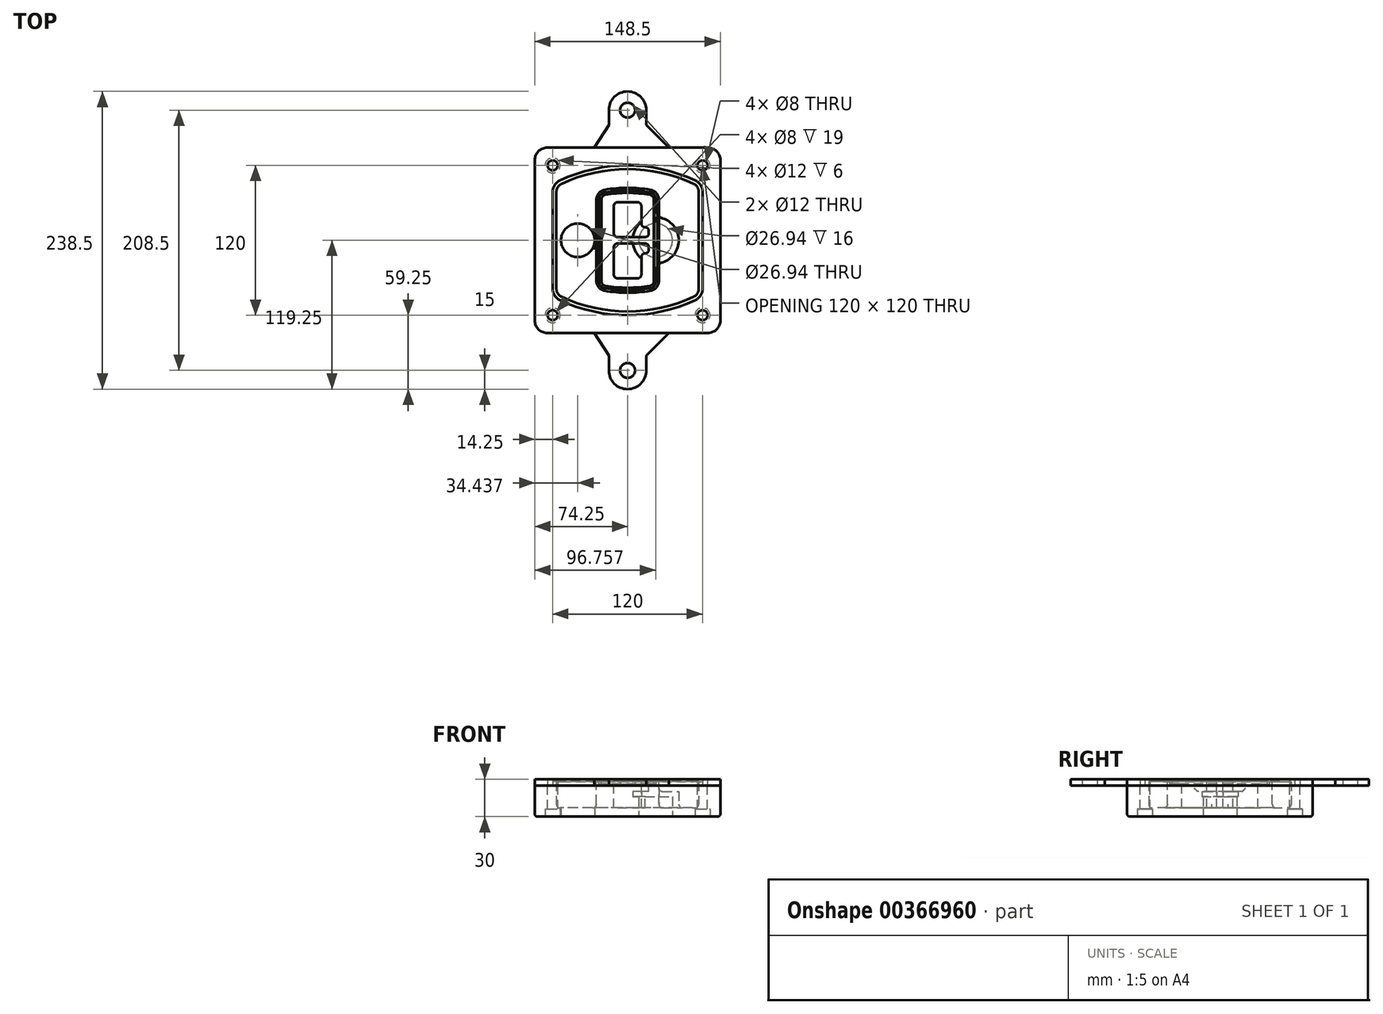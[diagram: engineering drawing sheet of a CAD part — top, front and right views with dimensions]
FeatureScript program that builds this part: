
annotation { "Feature Type Name" : "Feature", "Feature Type Description" : "" }
export const myFeature = defineFeature(function(context is Context, id is Id, definition is map)
    precondition{}
    {
        {
            var Q0;
            Q0=qCreatedBy(makeId("Top.planeOp"),FACE);
            var sketch = newSketch(context, id + "F0", { "sketchPlane" : qUnion([Q0])});
            skPoint(sketch, "E0.rect.middle", {"position": v(0, 0) * mm});
            skLineSegment(sketch, "E1.bottom", {"start": v(-64.25, -74.25) * mm, "end": v(64.25, -74.25) * mm});
            skLineSegment(sketch, "E1.top", {"start": v(-64.25, 74.25) * mm, "end": v(64.25, 74.25) * mm});
            skLineSegment(sketch, "E1.left", {"start": v(-74.25, -64.25) * mm, "end": v(-74.25, 64.25) * mm});
            skLineSegment(sketch, "E1.right", {"start": v(74.25, -64.25) * mm, "end": v(74.25, 64.25) * mm});
            skLineSegment(sketch, "E2", {"start": v(-74.25, 74.25) * mm, "end": v(74.25, -74.25) * mm, "construction": true});
            skLineSegment(sketch, "E3", {"start": v(74.25, 74.25) * mm, "end": v(-74.25, -74.25) * mm, "construction": true});
            skCircle(sketch, "E4", {"center": v(-60, 60) * mm, "radius": 4 * mm});
            skCircle(sketch, "E5", {"center": v(60, 60) * mm, "radius": 4 * mm});
            skCircle(sketch, "E6", {"center": v(60, -60) * mm, "radius": 4 * mm});
            skCircle(sketch, "E7", {"center": v(-60, -60) * mm, "radius": 4 * mm});
            skLineSegment(sketch, "E8", {"start": v(-60, 60) * mm, "end": v(60, 60) * mm, "construction": true});
            skLineSegment(sketch, "E9", {"start": v(60, 60) * mm, "end": v(60, -60) * mm, "construction": true});
            skLineSegment(sketch, "E10", {"start": v(60, -60) * mm, "end": v(-60, -60) * mm, "construction": true});
            skLineSegment(sketch, "E11", {"start": v(-60, -60) * mm, "end": v(-60, 60) * mm, "construction": true});
            skLineSegment(sketch, "E12", {"start": v(-60, 38.83) * mm, "end": v(-60, -38.83) * mm});
            skLineSegment(sketch, "E13", {"start": v(60, 38.83) * mm, "end": v(60, -38.83) * mm});
            skArc(sketch, "E14", {"start": v(54.26, 47.88) * mm, "mid": v(0, 60) * mm, "end": v(-54.26, 47.88) * mm});
            skArc(sketch, "E15", {"start": v(-54.26, -47.88) * mm, "mid": v(0, -60) * mm, "end": v(54.26, -47.88) * mm});
            skLineSegment(sketch, "E16", {"start": v(-60, 0) * mm, "end": v(60, 0) * mm, "construction": true});
            skPoint(sketch, "E17.visualSharp", {"position": v(-60, -45) * mm});
            skArc(sketch, "E17.filletArc", {"start": v(-60, -38.83) * mm, "mid": v(-58.44, -44.2) * mm, "end": v(-54.26, -47.88) * mm});
            skPoint(sketch, "E18.visualSharp", {"position": v(-60, 45) * mm});
            skArc(sketch, "E18.filletArc", {"start": v(-54.26, 47.88) * mm, "mid": v(-58.44, 44.2) * mm, "end": v(-60, 38.83) * mm});
            skPoint(sketch, "E19.visualSharp", {"position": v(60, 45) * mm});
            skArc(sketch, "E19.filletArc", {"start": v(60, 38.83) * mm, "mid": v(58.44, 44.2) * mm, "end": v(54.26, 47.88) * mm});
            skPoint(sketch, "E20.visualSharp", {"position": v(60, -45) * mm});
            skArc(sketch, "E20.filletArc", {"start": v(54.26, -47.88) * mm, "mid": v(58.44, -44.2) * mm, "end": v(60, -38.83) * mm});
            skPoint(sketch, "E21.visualSharp", {"position": v(-74.25, 74.25) * mm});
            skArc(sketch, "E21.filletArc", {"start": v(-64.25, 74.25) * mm, "mid": v(-71.32, 71.32) * mm, "end": v(-74.25, 64.25) * mm});
            skPoint(sketch, "E22.visualSharp", {"position": v(74.25, 74.25) * mm});
            skArc(sketch, "E22.filletArc", {"start": v(74.25, 64.25) * mm, "mid": v(71.32, 71.32) * mm, "end": v(64.25, 74.25) * mm});
            skPoint(sketch, "E23.visualSharp", {"position": v(74.25, -74.25) * mm});
            skArc(sketch, "E23.filletArc", {"start": v(64.25, -74.25) * mm, "mid": v(71.32, -71.32) * mm, "end": v(74.25, -64.25) * mm});
            skPoint(sketch, "E24.visualSharp", {"position": v(-74.25, -74.25) * mm});
            skArc(sketch, "E24.filletArc", {"start": v(-74.25, -64.25) * mm, "mid": v(-71.32, -71.32) * mm, "end": v(-64.25, -74.25) * mm});
            skArc(sketch, "E25.0", {"start": v(57, 38.83) * mm, "mid": v(55.9, 42.58) * mm, "end": v(52.98, 45.17) * mm});
            skLineSegment(sketch, "E25.1", {"start": v(57, 38.83) * mm, "end": v(57, -38.83) * mm});
            skArc(sketch, "E25.2", {"start": v(52.98, -45.17) * mm, "mid": v(55.9, -42.58) * mm, "end": v(57, -38.83) * mm});
            skArc(sketch, "E25.3", {"start": v(-52.98, -45.17) * mm, "mid": v(0, -57) * mm, "end": v(52.98, -45.17) * mm});
            skArc(sketch, "E25.4", {"start": v(-57, -38.83) * mm, "mid": v(-55.9, -42.58) * mm, "end": v(-52.98, -45.17) * mm});
            skArc(sketch, "E25.5", {"start": v(52.98, 45.17) * mm, "mid": v(0, 57) * mm, "end": v(-52.98, 45.17) * mm});
            skLineSegment(sketch, "E25.6", {"start": v(-57, 38.83) * mm, "end": v(-57, -38.83) * mm});
            skArc(sketch, "E25.7", {"start": v(-52.98, 45.17) * mm, "mid": v(-55.9, 42.58) * mm, "end": v(-57, 38.83) * mm});
            skArc(sketch, "E26.0", {"start": v(-55.96, 51.5) * mm, "mid": v(-61.82, 46.33) * mm, "end": v(-64, 38.83) * mm});
            skArc(sketch, "E26.1", {"start": v(55.96, 51.5) * mm, "mid": v(0, 64) * mm, "end": v(-55.96, 51.5) * mm});
            skArc(sketch, "E26.2", {"start": v(64, 38.83) * mm, "mid": v(61.82, 46.33) * mm, "end": v(55.96, 51.5) * mm});
            skLineSegment(sketch, "E26.3", {"start": v(64, 38.83) * mm, "end": v(64, -38.83) * mm});
            skArc(sketch, "E26.4", {"start": v(55.96, -51.5) * mm, "mid": v(61.82, -46.33) * mm, "end": v(64, -38.83) * mm});
            skLineSegment(sketch, "E26.5", {"start": v(-64, 38.83) * mm, "end": v(-64, -38.83) * mm});
            skArc(sketch, "E26.6", {"start": v(-55.96, -51.5) * mm, "mid": v(0, -64) * mm, "end": v(55.96, -51.5) * mm});
            skArc(sketch, "E26.7", {"start": v(-64, -38.83) * mm, "mid": v(-61.82, -46.33) * mm, "end": v(-55.96, -51.5) * mm});
            skSolve(sketch);
        }
        {
            var Q0;
            Q0=makeQuery(id+"F0.imprint","IMPRINT",FACE,{"disambiguationData":[TD([[makeQuery(id+"F0.imprint","IMPRINT",EDGE,{"derivedFrom":sQuery(id+"F0.wireOp",EDGE,"E1.bottom")}),1.0]])]});
            var Q1;
            Q1=makeQuery(id+"F0.imprint","IMPRINT",FACE,{"disambiguationData":[TD([[makeQuery(id+"F0.imprint","IMPRINT",EDGE,{"derivedFrom":sQuery(id+"F0.wireOp",EDGE,"E12")}),1.0]])]});
            var Q2;
            Q2=makeQuery(id+"F0.imprint","IMPRINT",FACE,{"disambiguationData":[TD([[makeQuery(id+"F0.imprint","IMPRINT",EDGE,{"derivedFrom":sQuery(id+"F0.wireOp",EDGE,"E25.0")}),1.0]])]});
            var Q3;
            Q3=makeQuery(id+"F0.imprint","IMPRINT",FACE,{"disambiguationData":[TD([[makeQuery(id+"F0.imprint","IMPRINT",EDGE,{"derivedFrom":sQuery(id+"F0.wireOp",EDGE,"E12")}),-1.0]])]});
            extrude(context, id + "F1", {"entities" : qUnion([Q0, Q1, Q2, Q3]), "oppositeDirection" : true, "depth" : 25 * mm});
        }
        {
            var Q0;
            Q0=makeQuery(id+"F0.imprint","IMPRINT",FACE,{"disambiguationData":[TD([[makeQuery(id+"F0.imprint","IMPRINT",EDGE,{"derivedFrom":sQuery(id+"F0.wireOp",EDGE,"E12")}),1.0]])]});
            extrude(context, id + "F2", {"entities" : qUnion([Q0]), "operationType" : NewBodyOperationType.ADD, "depth" : 3 * mm});
        }
        {
            var Q0;
            Q0=makeQuery(id+"F0.imprint","IMPRINT",FACE,{"disambiguationData":[TD([[makeQuery(id+"F0.imprint","IMPRINT",EDGE,{"derivedFrom":sQuery(id+"F0.wireOp",EDGE,"E25.0")}),1.0]])]});
            extrude(context, id + "F3", {"entities" : qUnion([Q0]), "operationType" : NewBodyOperationType.REMOVE, "oppositeDirection" : true, "depth" : 18 * mm});
        }
        {
            var Q0;
            Q0=makeQuery(id+"F2.opExtrude","CAP_FACE",FACE,{"disambiguationData":[OSD([sQuery(id+"F0.wireOp",EDGE,"E12"),sQuery(id+"F0.wireOp",EDGE,"E13"),sQuery(id+"F0.wireOp",EDGE,"E14"),sQuery(id+"F0.wireOp",EDGE,"E15"),sQuery(id+"F0.wireOp",EDGE,"E17.filletArc"),sQuery(id+"F0.wireOp",EDGE,"E18.filletArc"),sQuery(id+"F0.wireOp",EDGE,"E19.filletArc"),sQuery(id+"F0.wireOp",EDGE,"E20.filletArc"),sQuery(id+"F0.wireOp",EDGE,"E25.0"),sQuery(id+"F0.wireOp",EDGE,"E25.1"),sQuery(id+"F0.wireOp",EDGE,"E25.2"),sQuery(id+"F0.wireOp",EDGE,"E25.3"),sQuery(id+"F0.wireOp",EDGE,"E25.4"),sQuery(id+"F0.wireOp",EDGE,"E25.5"),sQuery(id+"F0.wireOp",EDGE,"E25.6"),sQuery(id+"F0.wireOp",EDGE,"E25.7")])],"isStart":false});
            var sketch = newSketch(context, id + "F4", { "sketchPlane" : qUnion([Q0])});
            skArc(sketch, "E27.0", {"start": v(-18.34, -40.45) * mm, "mid": v(0, -42) * mm, "end": v(18.34, -40.45) * mm});
            skArc(sketch, "E28.0", {"start": v(18.34, 40.45) * mm, "mid": v(0, 42) * mm, "end": v(-18.34, 40.45) * mm});
            skLineSegment(sketch, "E29", {"start": v(-25, 32.57) * mm, "end": v(-25, -32.57) * mm});
            skLineSegment(sketch, "E30", {"start": v(25, 32.57) * mm, "end": v(25, -32.57) * mm});
            skLineSegment(sketch, "E31", {"start": v(-25, 39.1) * mm, "end": v(25, 39.1) * mm, "construction": true});
            skLineSegment(sketch, "E32", {"start": v(-25, -39.1) * mm, "end": v(25, -39.1) * mm, "construction": true});
            skPoint(sketch, "E33.visualSharp", {"position": v(-25, 39.1) * mm});
            skArc(sketch, "E33.filletArc", {"start": v(-18.34, 40.45) * mm, "mid": v(-23.11, 37.73) * mm, "end": v(-25, 32.57) * mm});
            skPoint(sketch, "E34.visualSharp", {"position": v(25, 39.1) * mm});
            skArc(sketch, "E34.filletArc", {"start": v(25, 32.57) * mm, "mid": v(23.11, 37.73) * mm, "end": v(18.34, 40.45) * mm});
            skPoint(sketch, "E35.visualSharp", {"position": v(25, -39.1) * mm});
            skArc(sketch, "E35.filletArc", {"start": v(18.34, -40.45) * mm, "mid": v(23.11, -37.73) * mm, "end": v(25, -32.57) * mm});
            skPoint(sketch, "E36.visualSharp", {"position": v(-25, -39.1) * mm});
            skArc(sketch, "E36.filletArc", {"start": v(-25, -32.57) * mm, "mid": v(-23.11, -37.73) * mm, "end": v(-18.34, -40.45) * mm});
            skArc(sketch, "E37.0", {"start": v(52.98, 45.17) * mm, "mid": v(0, 57) * mm, "end": v(-52.98, 45.17) * mm});
            skArc(sketch, "E37.1", {"start": v(-52.98, 45.17) * mm, "mid": v(-55.9, 42.58) * mm, "end": v(-57, 38.83) * mm});
            skLineSegment(sketch, "E37.2", {"start": v(-57, 38.83) * mm, "end": v(-57, -38.83) * mm});
            skArc(sketch, "E37.3", {"start": v(-57, -38.83) * mm, "mid": v(-55.9, -42.58) * mm, "end": v(-52.98, -45.17) * mm});
            skArc(sketch, "E37.4", {"start": v(-52.98, -45.17) * mm, "mid": v(0, -57) * mm, "end": v(52.98, -45.17) * mm});
            skArc(sketch, "E37.5", {"start": v(52.98, -45.17) * mm, "mid": v(55.9, -42.58) * mm, "end": v(57, -38.83) * mm});
            skLineSegment(sketch, "E37.6", {"start": v(57, 38.83) * mm, "end": v(57, -38.83) * mm});
            skArc(sketch, "E37.7", {"start": v(57, 38.83) * mm, "mid": v(55.9, 42.58) * mm, "end": v(52.98, 45.17) * mm});
            skLineSegment(sketch, "E38.0", {"start": v(23, 32.57) * mm, "end": v(23, -32.57) * mm});
            skArc(sketch, "E38.1", {"start": v(18, -38.48) * mm, "mid": v(21.58, -36.44) * mm, "end": v(23, -32.57) * mm});
            skArc(sketch, "E38.2", {"start": v(-18, -38.48) * mm, "mid": v(0, -40) * mm, "end": v(18, -38.48) * mm});
            skArc(sketch, "E38.3", {"start": v(-23, -32.57) * mm, "mid": v(-21.58, -36.44) * mm, "end": v(-18, -38.48) * mm});
            skLineSegment(sketch, "E38.4", {"start": v(-23, 32.57) * mm, "end": v(-23, -32.57) * mm});
            skArc(sketch, "E38.5", {"start": v(23, 32.57) * mm, "mid": v(21.58, 36.44) * mm, "end": v(18, 38.48) * mm});
            skArc(sketch, "E38.6", {"start": v(-18, 38.48) * mm, "mid": v(-21.58, 36.44) * mm, "end": v(-23, 32.57) * mm});
            skArc(sketch, "E38.7", {"start": v(18, 38.48) * mm, "mid": v(0, 40) * mm, "end": v(-18, 38.48) * mm});
            skArc(sketch, "E39.0", {"start": v(21, 32.57) * mm, "mid": v(20.06, 35.15) * mm, "end": v(17.67, 36.5) * mm});
            skLineSegment(sketch, "E39.1", {"start": v(21, 32.57) * mm, "end": v(21, -32.57) * mm});
            skArc(sketch, "E39.2", {"start": v(17.67, -36.5) * mm, "mid": v(20.06, -35.15) * mm, "end": v(21, -32.57) * mm});
            skArc(sketch, "E39.3", {"start": v(-17.67, -36.5) * mm, "mid": v(0, -38) * mm, "end": v(17.67, -36.5) * mm});
            skArc(sketch, "E39.4", {"start": v(-21, -32.57) * mm, "mid": v(-20.06, -35.15) * mm, "end": v(-17.67, -36.5) * mm});
            skArc(sketch, "E39.5", {"start": v(17.67, 36.5) * mm, "mid": v(0, 38) * mm, "end": v(-17.67, 36.5) * mm});
            skLineSegment(sketch, "E39.6", {"start": v(-21, 32.57) * mm, "end": v(-21, -32.57) * mm});
            skArc(sketch, "E39.7", {"start": v(-17.67, 36.5) * mm, "mid": v(-20.06, 35.15) * mm, "end": v(-21, 32.57) * mm});
            skLineSegment(sketch, "E40", {"start": v(-25, 0) * mm, "end": v(25, 0) * mm, "construction": true});
            skLineSegment(sketch, "E41", {"start": v(-11, 5.5) * mm, "end": v(-11, 27.5) * mm});
            skLineSegment(sketch, "E42", {"start": v(-8, 30.5) * mm, "end": v(8, 30.5) * mm});
            skLineSegment(sketch, "E43", {"start": v(11, 27.5) * mm, "end": v(11, 13.5) * mm});
            skLineSegment(sketch, "E44", {"start": v(14, 10.5) * mm, "end": v(14, 10.5) * mm});
            skLineSegment(sketch, "E45", {"start": v(17, 7.5) * mm, "end": v(17, 5.5) * mm});
            skLineSegment(sketch, "E46", {"start": v(14, 2.5) * mm, "end": v(-8, 2.5) * mm});
            skPoint(sketch, "E47.visualSharp", {"position": v(-11, 30.5) * mm});
            skArc(sketch, "E47.filletArc", {"start": v(-8, 30.5) * mm, "mid": v(-10.12, 29.62) * mm, "end": v(-11, 27.5) * mm});
            skPoint(sketch, "E48.visualSharp", {"position": v(11, 30.5) * mm});
            skArc(sketch, "E48.filletArc", {"start": v(11, 27.5) * mm, "mid": v(10.12, 29.62) * mm, "end": v(8, 30.5) * mm});
            skPoint(sketch, "E49.visualSharp", {"position": v(11, 10.5) * mm});
            skArc(sketch, "E49.filletArc", {"start": v(11, 13.5) * mm, "mid": v(11.88, 11.38) * mm, "end": v(14, 10.5) * mm});
            skPoint(sketch, "E50.visualSharp", {"position": v(17, 10.5) * mm});
            skArc(sketch, "E50.filletArc", {"start": v(17, 7.5) * mm, "mid": v(16.12, 9.62) * mm, "end": v(14, 10.5) * mm});
            skPoint(sketch, "E51.visualSharp", {"position": v(17, 2.5) * mm});
            skArc(sketch, "E51.filletArc", {"start": v(14, 2.5) * mm, "mid": v(16.12, 3.38) * mm, "end": v(17, 5.5) * mm});
            skPoint(sketch, "E52.visualSharp", {"position": v(-11, 2.5) * mm});
            skArc(sketch, "E52.filletArc", {"start": v(-11, 5.5) * mm, "mid": v(-10.12, 3.38) * mm, "end": v(-8, 2.5) * mm});
            skLineSegment(sketch, "E53.0.MirrorCS", {"start": v(14, -2.5) * mm, "end": v(-8, -2.5) * mm});
            skArc(sketch, "E54.0.MirrorCS", {"start": v(-11, -5.5) * mm, "mid": v(-10.12, -3.38) * mm, "end": v(-8, -2.5) * mm});
            skLineSegment(sketch, "E55.0.MirrorCS", {"start": v(-11, -5.5) * mm, "end": v(-11, -27.5) * mm});
            skArc(sketch, "E56.0.MirrorCS", {"start": v(-8, -30.5) * mm, "mid": v(-10.12, -29.62) * mm, "end": v(-11, -27.5) * mm});
            skLineSegment(sketch, "E57.0.MirrorCS", {"start": v(-8, -30.5) * mm, "end": v(8, -30.5) * mm});
            skArc(sketch, "E58.0.MirrorCS", {"start": v(11, -27.5) * mm, "mid": v(10.12, -29.62) * mm, "end": v(8, -30.5) * mm});
            skLineSegment(sketch, "E59.0.MirrorCS", {"start": v(11, -27.5) * mm, "end": v(11, -13.5) * mm});
            skArc(sketch, "E60.0.MirrorCS", {"start": v(11, -13.5) * mm, "mid": v(11.88, -11.38) * mm, "end": v(14, -10.5) * mm});
            skArc(sketch, "E61.0.MirrorCS", {"start": v(17, -7.5) * mm, "mid": v(16.12, -9.62) * mm, "end": v(14, -10.5) * mm});
            skLineSegment(sketch, "E62.0.MirrorCS", {"start": v(17, -7.5) * mm, "end": v(17, -5.5) * mm});
            skArc(sketch, "E63.0.MirrorCS", {"start": v(14, -2.5) * mm, "mid": v(16.12, -3.38) * mm, "end": v(17, -5.5) * mm});
            skSolve(sketch);
        }
        {
            var Q0;
            Q0=makeQuery(id+"F4.imprint","IMPRINT",FACE,{"disambiguationData":[TD([[makeQuery(id+"F4.imprint","IMPRINT",EDGE,{"derivedFrom":sQuery(id+"F4.wireOp",EDGE,"E27.0")}),1.0]])]});
            var Q1;
            Q1=makeQuery(id+"F4.imprint","IMPRINT",FACE,{"disambiguationData":[TD([[makeQuery(id+"F4.imprint","IMPRINT",EDGE,{"derivedFrom":sQuery(id+"F4.wireOp",EDGE,"E38.0")}),-1.0]])]});
            var Q2;
            Q2=makeQuery(id+"F4.imprint","IMPRINT",FACE,{"disambiguationData":[TD([[makeQuery(id+"F4.imprint","IMPRINT",EDGE,{"derivedFrom":sQuery(id+"F4.wireOp",EDGE,"E39.0")}),1.0]])]});
            extrude(context, id + "F5", {"entities" : qUnion([Q0, Q1, Q2]), "operationType" : NewBodyOperationType.ADD, "endBound" : BoundingType.UP_TO_NEXT, "oppositeDirection" : true, "depth" : 25 * mm});
        }
        {
            var Q0;
            Q0=makeQuery(id+"F4.imprint","IMPRINT",FACE,{"disambiguationData":[TD([[makeQuery(id+"F4.imprint","IMPRINT",EDGE,{"derivedFrom":sQuery(id+"F4.wireOp",EDGE,"E38.0")}),-1.0]])]});
            extrude(context, id + "F6", {"entities" : qUnion([Q0]), "operationType" : NewBodyOperationType.REMOVE, "oppositeDirection" : true, "depth" : 2 * mm});
        }
        {
            var Q0;
            Q0=makeQuery(id+"F1.opExtrude","CAP_FACE",FACE,{"disambiguationData":[OSD([sQuery(id+"F0.wireOp",EDGE,"E1.bottom"),sQuery(id+"F0.wireOp",EDGE,"E1.top"),sQuery(id+"F0.wireOp",EDGE,"E1.left"),sQuery(id+"F0.wireOp",EDGE,"E1.right"),sQuery(id+"F0.wireOp",EDGE,"E4"),sQuery(id+"F0.wireOp",EDGE,"E5"),sQuery(id+"F0.wireOp",EDGE,"E6"),sQuery(id+"F0.wireOp",EDGE,"E7"),sQuery(id+"F0.wireOp",EDGE,"E21.filletArc"),sQuery(id+"F0.wireOp",EDGE,"E22.filletArc"),sQuery(id+"F0.wireOp",EDGE,"E23.filletArc"),sQuery(id+"F0.wireOp",EDGE,"E24.filletArc")])],"isStart":false});
            var sketch = newSketch(context, id + "F7", { "sketchPlane" : qUnion([Q0])});
            skCircle(sketch, "E64", {"center": v(22.5, 0) * mm, "radius": 13.47 * mm});
            skCircle(sketch, "E65", {"center": v(-39.81, 0) * mm, "radius": 13.47 * mm});
            skLineSegment(sketch, "E66", {"start": v(74.25, 0) * mm, "end": v(-74.25, 0) * mm});
            skCircle(sketch, "E67", {"center": v(22.5, 0) * mm, "radius": 18.47 * mm});
            skCircle(sketch, "E68", {"center": v(60, -60) * mm, "radius": 6 * mm});
            skCircle(sketch, "E69", {"center": v(-60, -60) * mm, "radius": 6 * mm});
            skCircle(sketch, "E70", {"center": v(-60, 60) * mm, "radius": 6 * mm});
            skCircle(sketch, "E71", {"center": v(60, 60) * mm, "radius": 6 * mm});
            skSolve(sketch);
        }
        {
            var Q0;
            {var subQ1=sQuery(id+"F7.wireOp",EDGE,"E66");var subQ4=sQuery(id+"F7.wireOp",EDGE,"E64");var subQ6=makeQuery(id+"F7.imprint","INTERSECT",VERTEX,{"disambiguationData":[OD(0.0)],"derivedFrom":[subQ4,subQ1]});Q0=makeQuery(id+"F7.imprint","IMPRINT",FACE,{"disambiguationData":[TD([[makeQuery(id+"F7.imprint","IMPRINT",EDGE,{"disambiguationData":[TD([[subQ6,-1.0]])],"derivedFrom":subQ4}),-1.0]])]});}
            var Q1;
            {var subQ0=sQuery(id+"F7.wireOp",EDGE,"E66");var subQ1=sQuery(id+"F7.wireOp",EDGE,"E64");var subQ3=makeQuery(id+"F7.imprint","INTERSECT",VERTEX,{"disambiguationData":[OD(0.0)],"derivedFrom":[subQ1,subQ0]});Q1=makeQuery(id+"F7.imprint","IMPRINT",FACE,{"disambiguationData":[TD([[makeQuery(id+"F7.imprint","IMPRINT",EDGE,{"disambiguationData":[TD([[subQ3,-1.0]])],"derivedFrom":subQ1}),1.0]])]});}
            var Q2;
            {var subQ0=sQuery(id+"F7.wireOp",EDGE,"E66");var subQ1=sQuery(id+"F7.wireOp",EDGE,"E64");var subQ3=makeQuery(id+"F7.imprint","INTERSECT",VERTEX,{"disambiguationData":[OD(0.0)],"derivedFrom":[subQ1,subQ0]});Q2=makeQuery(id+"F7.imprint","IMPRINT",FACE,{"disambiguationData":[TD([[makeQuery(id+"F7.imprint","IMPRINT",EDGE,{"disambiguationData":[TD([[subQ3,1.0]])],"derivedFrom":subQ1}),1.0]])]});}
            var Q3;
            {var subQ1=sQuery(id+"F7.wireOp",EDGE,"E66");var subQ4=sQuery(id+"F7.wireOp",EDGE,"E64");var subQ6=makeQuery(id+"F7.imprint","INTERSECT",VERTEX,{"disambiguationData":[OD(0.0)],"derivedFrom":[subQ4,subQ1]});Q3=makeQuery(id+"F7.imprint","IMPRINT",FACE,{"disambiguationData":[TD([[makeQuery(id+"F7.imprint","IMPRINT",EDGE,{"disambiguationData":[TD([[subQ6,1.0]])],"derivedFrom":subQ4}),-1.0]])]});}
            extrude(context, id + "F8", {"entities" : qUnion([Q0, Q1, Q2, Q3]), "operationType" : NewBodyOperationType.ADD, "oppositeDirection" : true, "depth" : 20 * mm});
        }
        {
            var Q0;
            {var subQ0=sQuery(id+"F7.wireOp",EDGE,"E66");var subQ1=sQuery(id+"F7.wireOp",EDGE,"E64");var subQ3=makeQuery(id+"F7.imprint","INTERSECT",VERTEX,{"disambiguationData":[OD(0.0)],"derivedFrom":[subQ1,subQ0]});Q0=makeQuery(id+"F7.imprint","IMPRINT",FACE,{"disambiguationData":[TD([[makeQuery(id+"F7.imprint","IMPRINT",EDGE,{"disambiguationData":[TD([[subQ3,-1.0]])],"derivedFrom":subQ1}),1.0]])]});}
            var Q1;
            {var subQ0=sQuery(id+"F7.wireOp",EDGE,"E66");var subQ1=sQuery(id+"F7.wireOp",EDGE,"E64");var subQ3=makeQuery(id+"F7.imprint","INTERSECT",VERTEX,{"disambiguationData":[OD(0.0)],"derivedFrom":[subQ1,subQ0]});Q1=makeQuery(id+"F7.imprint","IMPRINT",FACE,{"disambiguationData":[TD([[makeQuery(id+"F7.imprint","IMPRINT",EDGE,{"disambiguationData":[TD([[subQ3,1.0]])],"derivedFrom":subQ1}),1.0]])]});}
            extrude(context, id + "F9", {"entities" : qUnion([Q0, Q1]), "operationType" : NewBodyOperationType.REMOVE, "oppositeDirection" : true, "depth" : 16 * mm});
        }
        {
            var Q0;
            {var subQ0=sQuery(id+"F7.wireOp",EDGE,"E66");var subQ1=sQuery(id+"F7.wireOp",EDGE,"E65");var subQ3=makeQuery(id+"F7.imprint","INTERSECT",VERTEX,{"disambiguationData":[OD(0.0)],"derivedFrom":[subQ1,subQ0]});Q0=makeQuery(id+"F7.imprint","IMPRINT",FACE,{"disambiguationData":[TD([[makeQuery(id+"F7.imprint","IMPRINT",EDGE,{"disambiguationData":[TD([[subQ3,-1.0]])],"derivedFrom":subQ1}),1.0]])]});}
            var Q1;
            {var subQ0=sQuery(id+"F7.wireOp",EDGE,"E66");var subQ1=sQuery(id+"F7.wireOp",EDGE,"E65");var subQ3=makeQuery(id+"F7.imprint","INTERSECT",VERTEX,{"disambiguationData":[OD(0.0)],"derivedFrom":[subQ1,subQ0]});Q1=makeQuery(id+"F7.imprint","IMPRINT",FACE,{"disambiguationData":[TD([[makeQuery(id+"F7.imprint","IMPRINT",EDGE,{"disambiguationData":[TD([[subQ3,1.0]])],"derivedFrom":subQ1}),1.0]])]});}
            extrude(context, id + "F10", {"entities" : qUnion([Q0, Q1]), "operationType" : NewBodyOperationType.REMOVE, "oppositeDirection" : true, "depth" : 25 * mm});
        }
        {
            var Q0;
            Q0=makeQuery(id+"F7.imprint","IMPRINT",FACE,{"disambiguationData":[TD([[makeQuery(id+"F7.imprint","IMPRINT",EDGE,{"derivedFrom":sQuery(id+"F7.wireOp",EDGE,"E68")}),1.0]])]});
            var Q1;
            Q1=makeQuery(id+"F7.imprint","IMPRINT",FACE,{"disambiguationData":[TD([[makeQuery(id+"F7.imprint","IMPRINT",EDGE,{"derivedFrom":makeQuery(id+"F1.opExtrude","CAP_EDGE",EDGE,{"disambiguationData":[OSD([sQuery(id+"F0.wireOp",EDGE,"E5")])],"isStart":false})}),-1.0]])]});
            var Q2;
            Q2=makeQuery(id+"F7.imprint","IMPRINT",FACE,{"disambiguationData":[TD([[makeQuery(id+"F7.imprint","IMPRINT",EDGE,{"derivedFrom":sQuery(id+"F7.wireOp",EDGE,"E69")}),1.0]])]});
            var Q3;
            Q3=makeQuery(id+"F7.imprint","IMPRINT",FACE,{"disambiguationData":[TD([[makeQuery(id+"F7.imprint","IMPRINT",EDGE,{"derivedFrom":makeQuery(id+"F1.opExtrude","CAP_EDGE",EDGE,{"disambiguationData":[OSD([sQuery(id+"F0.wireOp",EDGE,"E4")])],"isStart":false})}),-1.0]])]});
            var Q4;
            Q4=makeQuery(id+"F7.imprint","IMPRINT",FACE,{"disambiguationData":[TD([[makeQuery(id+"F7.imprint","IMPRINT",EDGE,{"derivedFrom":sQuery(id+"F7.wireOp",EDGE,"E70")}),1.0]])]});
            var Q5;
            Q5=makeQuery(id+"F7.imprint","IMPRINT",FACE,{"disambiguationData":[TD([[makeQuery(id+"F7.imprint","IMPRINT",EDGE,{"derivedFrom":makeQuery(id+"F1.opExtrude","CAP_EDGE",EDGE,{"disambiguationData":[OSD([sQuery(id+"F0.wireOp",EDGE,"E7")])],"isStart":false})}),-1.0]])]});
            var Q6;
            Q6=makeQuery(id+"F7.imprint","IMPRINT",FACE,{"disambiguationData":[TD([[makeQuery(id+"F7.imprint","IMPRINT",EDGE,{"derivedFrom":sQuery(id+"F7.wireOp",EDGE,"E71")}),1.0]])]});
            var Q7;
            Q7=makeQuery(id+"F7.imprint","IMPRINT",FACE,{"disambiguationData":[TD([[makeQuery(id+"F7.imprint","IMPRINT",EDGE,{"derivedFrom":makeQuery(id+"F1.opExtrude","CAP_EDGE",EDGE,{"disambiguationData":[OSD([sQuery(id+"F0.wireOp",EDGE,"E6")])],"isStart":false})}),-1.0]])]});
            extrude(context, id + "F11", {"entities" : qUnion([Q0, Q1, Q2, Q3, Q4, Q5, Q6, Q7]), "operationType" : NewBodyOperationType.REMOVE, "oppositeDirection" : true, "depth" : 6 * mm});
        }
        {
            var Q0;
            Q0=makeQuery(id+"F9.boolean.opBoolean","COPY",FACE,{"derivedFrom":makeQuery(id+"F9.opExtrude","CAP_FACE",FACE,{"disambiguationData":[OSD([sQuery(id+"F7.wireOp",EDGE,"E64")])],"isStart":false})});
            var sketch = newSketch(context, id + "F12", { "sketchPlane" : qUnion([Q0])});
            skArc(sketch, "E72.0", {"start": v(11, 14.45) * mm, "mid": v(6.45, 9.13) * mm, "end": v(4.2, 2.5) * mm});
            skArc(sketch, "E72.1", {"start": v(4.2, -2.5) * mm, "mid": v(6.45, -9.13) * mm, "end": v(11, -14.45) * mm});
            skLineSegment(sketch, "E73", {"start": v(4.2, -2.5) * mm, "end": v(14, -2.5) * mm});
            skLineSegment(sketch, "E74.0", {"start": v(14, 2.5) * mm, "end": v(4.2, 2.5) * mm});
            skArc(sketch, "E74.1", {"start": v(14, 2.5) * mm, "mid": v(16.12, 3.38) * mm, "end": v(17, 5.5) * mm});
            skLineSegment(sketch, "E74.2", {"start": v(17, 7.5) * mm, "end": v(17, 5.5) * mm});
            skArc(sketch, "E74.3", {"start": v(17, 7.5) * mm, "mid": v(16.12, 9.62) * mm, "end": v(14, 10.5) * mm});
            skArc(sketch, "E74.4", {"start": v(11, 13.5) * mm, "mid": v(11.88, 11.38) * mm, "end": v(14, 10.5) * mm});
            skLineSegment(sketch, "E74.5", {"start": v(11, 14.45) * mm, "end": v(11, 13.5) * mm});
            skLineSegment(sketch, "E74.7", {"start": v(14, -2.5) * mm, "end": v(4.2, -2.5) * mm});
            skArc(sketch, "E74.8", {"start": v(14, -2.5) * mm, "mid": v(16.12, -3.38) * mm, "end": v(17, -5.5) * mm});
            skLineSegment(sketch, "E74.9", {"start": v(17, -7.5) * mm, "end": v(17, -5.5) * mm});
            skArc(sketch, "E74.10", {"start": v(17, -7.5) * mm, "mid": v(16.12, -9.62) * mm, "end": v(14, -10.5) * mm});
            skArc(sketch, "E74.11", {"start": v(11, -13.5) * mm, "mid": v(11.88, -11.38) * mm, "end": v(14, -10.5) * mm});
            skLineSegment(sketch, "E74.12", {"start": v(11, -14.45) * mm, "end": v(11, -13.5) * mm});
            skPoint(sketch, "E75.orphan", {"position": v(11, -27.5) * mm});
            skPoint(sketch, "E76.orphan", {"position": v(-8, -2.5) * mm});
            skPoint(sketch, "E77.orphan", {"position": v(-8, 2.5) * mm});
            skPoint(sketch, "E78.orphan", {"position": v(11, 27.5) * mm});
            skSolve(sketch);
        }
        {
            var Q0;
            {var subQ7=sQuery(id+"F12.wireOp",EDGE,"E72.0");var subQ14=sQuery(id+"F12.wireOp",EDGE,"E72.1");var subQ16=sQuery(id+"F12.wireOp",EDGE,"E74.1");var subQ18=sQuery(id+"F12.wireOp",EDGE,"E74.8");Q0=qUnion([makeQuery(id+"F12.imprint","IMPRINT",FACE,{"disambiguationData":[TD([[makeQuery(id+"F12.imprint","IMPRINT",EDGE,{"derivedFrom":subQ7}),1.0]])]}),makeQuery(id+"F12.imprint","IMPRINT",FACE,{"disambiguationData":[TD([[makeQuery(id+"F12.imprint","IMPRINT",EDGE,{"derivedFrom":subQ14}),1.0]])]}),makeQuery(id+"F12.imprint","IMPRINT",FACE,{"disambiguationData":[TD([[makeQuery(id+"F12.imprint","IMPRINT",EDGE,{"derivedFrom":subQ16}),1.0]])]}),makeQuery(id+"F12.imprint","IMPRINT",FACE,{"disambiguationData":[TD([[makeQuery(id+"F12.imprint","IMPRINT",EDGE,{"derivedFrom":subQ18}),-1.0]])]})]);}
            var Q1;
            Q1=makeQuery(id+"F5.boolean.opBoolean","SPLIT",FACE,{"disambiguationData":[TD([makeQuery(id+"F5.opExtrude","SWEPT_FACE",FACE,{"disambiguationData":[OSD([sQuery(id+"F4.wireOp",EDGE,"E41")])]})])],"derivedFrom":makeQuery(id+"F3.boolean.opBoolean","COPY",FACE,{"derivedFrom":makeQuery(id+"F3.opExtrude","CAP_FACE",FACE,{"disambiguationData":[OSD([sQuery(id+"F0.wireOp",EDGE,"E25.0"),sQuery(id+"F0.wireOp",EDGE,"E25.1"),sQuery(id+"F0.wireOp",EDGE,"E25.2"),sQuery(id+"F0.wireOp",EDGE,"E25.3"),sQuery(id+"F0.wireOp",EDGE,"E25.4"),sQuery(id+"F0.wireOp",EDGE,"E25.5"),sQuery(id+"F0.wireOp",EDGE,"E25.6"),sQuery(id+"F0.wireOp",EDGE,"E25.7")])],"isStart":false})})});
            extrude(context, id + "F13", {"entities" : qUnion([Q0]), "operationType" : NewBodyOperationType.REMOVE, "endBound" : BoundingType.UP_TO_SURFACE, "endBoundEntityFace" : qUnion([Q1]), "depth" : 25 * mm});
        }
        {
            var Q0;
            Q0=makeQuery(id+"F3.boolean.opBoolean","COPY",EDGE,{"derivedFrom":makeQuery(id+"F3.opExtrude","CAP_EDGE",EDGE,{"disambiguationData":[OSD([sQuery(id+"F0.wireOp",EDGE,"E25.6")])],"isStart":false})});
            var Q1;
            Q1=makeQuery(id+"F8.boolean.opBoolean","INTERSECT",EDGE,{"derivedFrom":[makeQuery(id+"F5.opExtrude","SWEPT_FACE",FACE,{"disambiguationData":[OSD([sQuery(id+"F4.wireOp",EDGE,"E30")])]}),makeQuery(id+"F8.opExtrude","CAP_FACE",FACE,{"disambiguationData":[OSD([sQuery(id+"F7.wireOp",EDGE,"E67")])],"isStart":false})]});
            var Q2;
            Q2=makeQuery(id+"F8.boolean.opBoolean","INTERSECT",EDGE,{"disambiguationData":[OD(1.0)],"derivedFrom":[makeQuery(id+"F5.opExtrude","SWEPT_FACE",FACE,{"disambiguationData":[OSD([sQuery(id+"F4.wireOp",EDGE,"E30")])]}),makeQuery(id+"F8.opExtrude","SWEPT_FACE",FACE,{"disambiguationData":[OSD([sQuery(id+"F7.wireOp",EDGE,"E67")])]})]});
            var Q3;
            {var subQ0=sQuery(id+"F4.wireOp",EDGE,"E30");Q3=makeQuery(id+"F8.boolean.opBoolean","SPLIT",EDGE,{"disambiguationData":[TD([makeQuery(id+"F5.opExtrude","SWEPT_FACE",FACE,{"disambiguationData":[OSD([sQuery(id+"F4.wireOp",EDGE,"E35.filletArc")])]})])],"derivedFrom":makeQuery(id+"F5.opExtrude","CAP_EDGE",EDGE,{"disambiguationData":[OSD([subQ0])],"isStart":false})});}
            var Q4;
            {var subQ0=sQuery(id+"F0.wireOp",EDGE,"E25.7");var subQ1=sQuery(id+"F0.wireOp",EDGE,"E25.1");var subQ2=sQuery(id+"F0.wireOp",EDGE,"E25.6");var subQ3=sQuery(id+"F0.wireOp",EDGE,"E25.5");var subQ4=sQuery(id+"F0.wireOp",EDGE,"E25.4");var subQ5=sQuery(id+"F0.wireOp",EDGE,"E25.0");var subQ6=sQuery(id+"F0.wireOp",EDGE,"E25.2");var subQ7=sQuery(id+"F0.wireOp",EDGE,"E25.3");Q4=makeQuery(id+"F8.boolean.opBoolean","INTERSECT",EDGE,{"derivedFrom":[makeQuery(id+"F5.boolean.opBoolean","SPLIT",FACE,{"disambiguationData":[TD([makeQuery(id+"F2.opExtrude","SWEPT_FACE",FACE,{"disambiguationData":[OSD([subQ5])]})])],"derivedFrom":makeQuery(id+"F3.boolean.opBoolean","COPY",FACE,{"derivedFrom":makeQuery(id+"F3.opExtrude","CAP_FACE",FACE,{"disambiguationData":[OSD([subQ5,subQ1,subQ6,subQ7,subQ4,subQ3,subQ2,subQ0])],"isStart":false})})}),makeQuery(id+"F8.opExtrude","SWEPT_FACE",FACE,{"disambiguationData":[OSD([sQuery(id+"F7.wireOp",EDGE,"E67")])]})]});}
            var Q5;
            Q5=makeQuery(id+"F8.boolean.opBoolean","INTERSECT",EDGE,{"disambiguationData":[OD(0.0)],"derivedFrom":[makeQuery(id+"F5.opExtrude","SWEPT_FACE",FACE,{"disambiguationData":[OSD([sQuery(id+"F4.wireOp",EDGE,"E30")])]}),makeQuery(id+"F8.opExtrude","SWEPT_FACE",FACE,{"disambiguationData":[OSD([sQuery(id+"F7.wireOp",EDGE,"E67")])]})]});
            fillet(context, id + "F14", {"entities" : qUnion([Q0, Q1, Q2, Q3, Q4, Q5]), "radius" : 3 * mm, "tangentPropagation" : true, "allowEdgeOverflow" : false});
        }
        {
            var Q0;
            Q0=makeQuery(id+"F1.opExtrude","CAP_EDGE",EDGE,{"disambiguationData":[OSD([sQuery(id+"F0.wireOp",EDGE,"E1.bottom")])],"isStart":false});
            fillet(context, id + "F15", {"entities" : qUnion([Q0]), "radius" : 2 * mm, "tangentPropagation" : true, "allowEdgeOverflow" : false});
        }
        {
            var Q0;
            {var subQ0=sQuery(id+"F0.wireOp",EDGE,"E21.filletArc");var subQ1=sQuery(id+"F0.wireOp",EDGE,"E7");var subQ2=sQuery(id+"F0.wireOp",EDGE,"E6");var subQ3=sQuery(id+"F0.wireOp",EDGE,"E5");var subQ4=sQuery(id+"F0.wireOp",EDGE,"E4");var subQ5=sQuery(id+"F0.wireOp",EDGE,"E22.filletArc");var subQ6=sQuery(id+"F0.wireOp",EDGE,"E1.bottom");var subQ7=sQuery(id+"F0.wireOp",EDGE,"E1.right");var subQ8=sQuery(id+"F0.wireOp",EDGE,"E1.top");var subQ9=sQuery(id+"F0.wireOp",EDGE,"E1.left");var subQ10=sQuery(id+"F0.wireOp",EDGE,"E23.filletArc");var subQ11=sQuery(id+"F0.wireOp",EDGE,"E24.filletArc");Q0=makeQuery(id+"F2.boolean.opBoolean","SPLIT",FACE,{"disambiguationData":[TD([makeQuery(id+"F1.opExtrude","SWEPT_FACE",FACE,{"disambiguationData":[OSD([subQ6])]})])],"derivedFrom":makeQuery(id+"F1.opExtrude","CAP_FACE",FACE,{"disambiguationData":[OSD([subQ6,subQ8,subQ9,subQ7,subQ4,subQ3,subQ2,subQ1,subQ0,subQ5,subQ10,subQ11])],"isStart":true})});}
            var sketch = newSketch(context, id + "F16", { "sketchPlane" : qUnion([Q0])});
            skSolve(sketch);
        }
        {
            var Q0;
            Q0=makeQuery(id+"F16.imprint","IMPRINT",FACE,{"disambiguationData":[TD([[makeQuery(id+"F16.imprint","IMPRINT",EDGE,{"derivedFrom":makeQuery(id+"F1.opExtrude","CAP_EDGE",EDGE,{"disambiguationData":[OSD([sQuery(id+"F0.wireOp",EDGE,"E1.bottom")])],"isStart":true})}),1.0]])]});
            var sketch = newSketch(context, id + "F17", { "sketchPlane" : qUnion([Q0])});
            skCircle(sketch, "E79", {"center": v(0, 104.25) * mm, "radius": 6 * mm});
            skLineSegment(sketch, "E80", {"start": v(-15, 104.25) * mm, "end": v(-15, 92.25) * mm});
            skLineSegment(sketch, "E81", {"start": v(-15, 92.25) * mm, "end": v(-26.84, 74.1) * mm});
            skLineSegment(sketch, "E82", {"start": v(15, 104.25) * mm, "end": v(15, 92.25) * mm});
            skLineSegment(sketch, "E83", {"start": v(0, 74.1) * mm, "end": v(0, 104.25) * mm, "construction": true});
            skArc(sketch, "E84", {"start": v(15, 104.25) * mm, "mid": v(0, 119.25) * mm, "end": v(-15, 104.25) * mm});
            skLineSegment(sketch, "E85", {"start": v(15, 92.25) * mm, "end": v(33.32, 73.93) * mm});
            skLineSegment(sketch, "E86", {"start": v(74.16, 0) * mm, "end": v(-74.16, 0) * mm, "construction": true});
            skLineSegment(sketch, "E87.MirrorCS", {"start": v(-15, -92.25) * mm, "end": v(-26.84, -74.1) * mm});
            skLineSegment(sketch, "E88.MirrorCS", {"start": v(-15, -104.25) * mm, "end": v(-15, -92.25) * mm});
            skArc(sketch, "E89.MirrorCS", {"start": v(15, -104.25) * mm, "mid": v(0, -119.25) * mm, "end": v(-15, -104.25) * mm});
            skCircle(sketch, "E90.MirrorC", {"center": v(0, -104.25) * mm, "radius": 6 * mm});
            skLineSegment(sketch, "E91.MirrorCS", {"start": v(0, -74.1) * mm, "end": v(0, -104.25) * mm, "construction": true});
            skLineSegment(sketch, "E92.MirrorCS", {"start": v(15, -104.25) * mm, "end": v(15, -92.25) * mm});
            skLineSegment(sketch, "E93.MirrorCS", {"start": v(15, -92.25) * mm, "end": v(33.32, -73.93) * mm});
            skSolve(sketch);
        }
        {
            var Q0;
            Q0=makeQuery(id+"F17.imprint","IMPRINT",FACE,{"disambiguationData":[TD([[makeQuery(id+"F17.imprint","IMPRINT",EDGE,{"derivedFrom":sQuery(id+"F17.wireOp",EDGE,"E79")}),-1.0]])]});
            var Q1;
            {var subQ0=sQuery(id+"F17.wireOp",EDGE,"E88.MirrorCS");Q1=makeQuery(id+"F17.imprint","IMPRINT",FACE,{"disambiguationData":[TD([[makeQuery(id+"F17.imprint","IMPRINT",EDGE,{"derivedFrom":subQ0}),-1.0]])]});}
            extrude(context, id + "F18", {"entities" : qUnion([Q0, Q1]), "depth" : 5 * mm});
        }
        {
            var Q0;
            Q0=makeQuery(id+"F16.imprint","IMPRINT",FACE,{"disambiguationData":[TD([[makeQuery(id+"F16.imprint","IMPRINT",EDGE,{"derivedFrom":makeQuery(id+"F1.opExtrude","CAP_EDGE",EDGE,{"disambiguationData":[OSD([sQuery(id+"F0.wireOp",EDGE,"E1.bottom")])],"isStart":true})}),1.0]])]});
            var Q1;
            Q1=makeQuery(id+"F18.opExtrude","CAP_FACE",FACE,{"disambiguationData":[OSD([sQuery(id+"F0.wireOp",EDGE,"E1.bottom"),sQuery(id+"F17.wireOp",EDGE,"E87.MirrorCS"),sQuery(id+"F17.wireOp",EDGE,"E88.MirrorCS"),sQuery(id+"F17.wireOp",EDGE,"E89.MirrorCS"),sQuery(id+"F17.wireOp",EDGE,"E90.MirrorC"),sQuery(id+"F17.wireOp",EDGE,"E92.MirrorCS"),sQuery(id+"F17.wireOp",EDGE,"E93.MirrorCS")])],"isStart":false});
            extrude(context, id + "F19", {"entities" : qUnion([Q0]), "endBound" : BoundingType.UP_TO_SURFACE, "endBoundEntityFace" : qUnion([Q1]), "depth" : 25 * mm});
        }
    });
